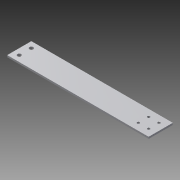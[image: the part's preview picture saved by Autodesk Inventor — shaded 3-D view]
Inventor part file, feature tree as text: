
AUTODESK INVENTOR PART (.ipt)
format: ipt  version: 2015 (Build 190159000, 159)  size: 127,488 bytes
history: native  units: mm
features: sketch x4, extrude x2, hole x2, other x1
ambient origin geometry x8: Origin, YZ Plane, XZ Plane, XY Plane, X Axis, Y Axis, Z Axis, Center Point
bodies: Body1 (feature_tree)
feature tree (9):
  other  "ソリッド1"
  extrude  "押し出し1"  Depth=112.0mm
  hole  "穴1"  [1 undecoded]
  extrude  "押し出し3"  Depth=1.5mm TaperAngle=0.0deg
  hole  "穴4"  [1 undecoded]
  sketch  "スケッチ1"
  sketch  "スケッチ3"
  sketch  "スケッチ7"
  sketch  "スケッチ8"
note: 2 required parameter values undecoded (feature->parameter linkage not recoverable at this tier; creation-order binding heuristic only, values carry confidence <= 0.55)
